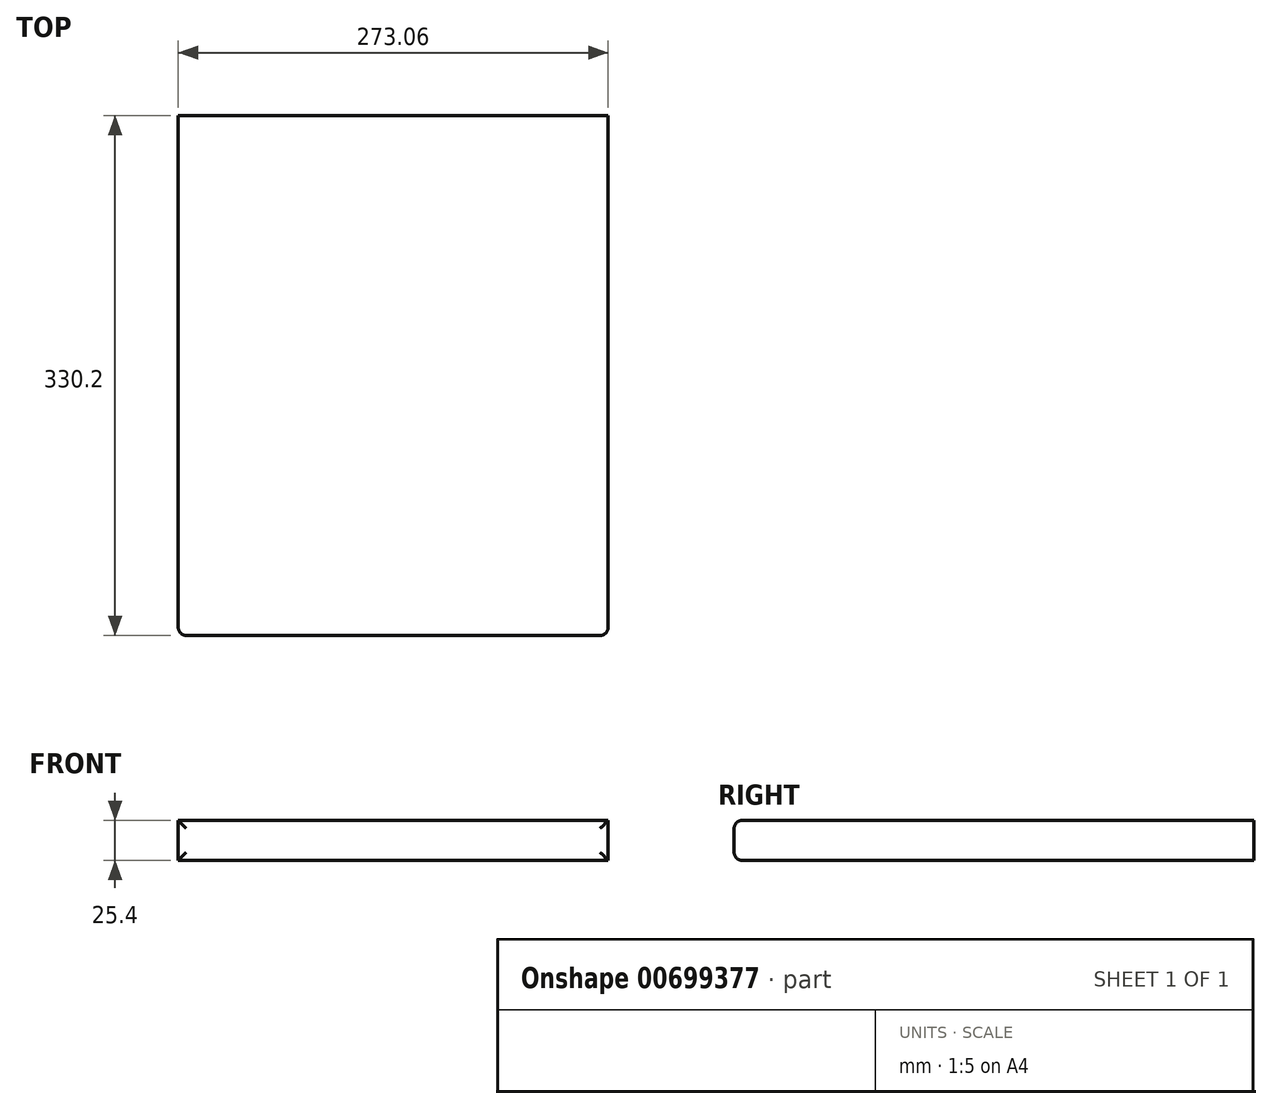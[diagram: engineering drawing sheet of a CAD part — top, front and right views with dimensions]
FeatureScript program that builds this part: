
annotation { "Feature Type Name" : "Feature", "Feature Type Description" : "" }
export const myFeature = defineFeature(function(context is Context, id is Id, definition is map)
    precondition{}
    {
        {
            var Q0;
            Q0=qCreatedBy(makeId("Front.planeOp"),FACE);
            var sketch = newSketch(context, id + "F0", { "sketchPlane" : qUnion([Q0])});
            skLineSegment(sketch, "E0.bottom", {"start": v(-136.52, 12.7) * mm, "end": v(136.53, 12.7) * mm});
            skLineSegment(sketch, "E0.top", {"start": v(-136.52, -12.7) * mm, "end": v(136.53, -12.7) * mm});
            skLineSegment(sketch, "E0.left", {"start": v(-136.52, 12.7) * mm, "end": v(-136.52, -12.7) * mm});
            skLineSegment(sketch, "E0.right", {"start": v(136.53, 12.7) * mm, "end": v(136.53, -12.7) * mm});
            skPoint(sketch, "E0.middle", {"position": v(0, 0) * mm});
            skSolve(sketch);
        }
        {
            var Q0;
            Q0=makeQuery(id+"F0.imprint","IMPRINT",FACE,{"disambiguationData":[TD([[makeQuery(id+"F0.imprint","IMPRINT",EDGE,{"derivedFrom":sQuery(id+"F0.wireOp",EDGE,"E0.bottom")}),-1.0]])]});
            extrude(context, id + "F1", {"entities" : qUnion([Q0]), "depth" : 330.2 * mm, "offsetDistance" : 25.4 * mm});
        }
        {
            var Q0;
            Q0=makeQuery(id+"F1.opExtrude","CAP_FACE",FACE,{"disambiguationData":[OSD([sQuery(id+"F0.wireOp",EDGE,"E0.bottom"),sQuery(id+"F0.wireOp",EDGE,"E0.top"),sQuery(id+"F0.wireOp",EDGE,"E0.left"),sQuery(id+"F0.wireOp",EDGE,"E0.right")])],"isStart":false});
            fillet(context, id + "F2", {"entities" : qUnion([Q0]), "radius" : 5.08 * mm, "tangentPropagation" : true, "allowEdgeOverflow" : false});
        }
    });
